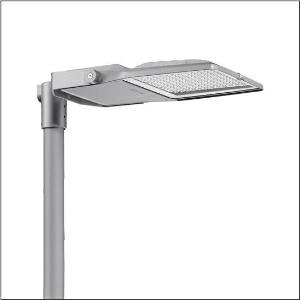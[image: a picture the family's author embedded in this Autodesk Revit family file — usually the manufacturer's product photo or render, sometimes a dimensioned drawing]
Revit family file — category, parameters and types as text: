
# Revit family: floodlight_fl_21_iq_midi___pl64_5xa7782f4e3a_0b41
name_source: partatom
category: Lighting Fixtures
units: mm (PartAtom-declared; Revit-internal decimal feet)

## family parameters
Cut with Voids When Loaded = No
Host = Face
Light Source = No
Part Type = Normal
Room Calculation Point = No
Round Connector Dimension = Use Diameter
Shared = No

## types (1)
- --- (1 x LED, 36050 lm, 270.2 W, 4000K)
    Apparent Load = 270 VA
    CIE Flux Codes = 28 80 98 100 100
    Color Rendering = 70
    Color Temperature = 4000K
    Default Elevation = 1800 mm
    Description = Floodlight FL 21 iQ midi, floodlight, primary light control with lens, of PMMA, primary optical cover: protective disc, of toughened safety glass, transparent, light distribution: PL64, light emission: direct distribution, installation type: surface-mounted, LED, High Power LED, rated luminous flux: 36.050lm, luminous efficacy: 133lm/W, light colour: 740, colour temperature: 4000K, control gear: ECG iQ, control: optimised constant luminous flux control (CLO 2.0), Desk-Remote (wireless, voltage-free reading and setting of iQ features in the workshop via application-optimized NFC function/RFID function), Smart-Wire, Night-Set, Temp-Guard, Auto-Match, Street-Remote, with terminal, 6-pole, mains connection: 220..240V, AC, 50/60Hz, start of lifetime: 270W, end of service life: 287W, reduction: 118W, luminaire housing, of diecast aluminium, powder-coated, Siteco® metallic grey (DB 702S), corrosivity category C5 mid according to DIN EN ISO 12944, sealing non-destructively replaceable, please order mast flange separately, mast bracket, of steel, galvanised, powder-coated, Siteco® metallic grey (DB 702S), protection rating (complete): IP66, insulation class (complete): insulation class II (safety insulation), certification: CE, ENEC, VDE, protection symbol: D, impact resistance: IK08, permissible operating ambient temperature: -40..+40°C, permissible operating ambient temperature for outdoor applications: -40..+50°C, standard: DIN EN 12944, LABS conformity tested according to VDMA 24364:2018-05, packaging unit: 1 piece

Light Distribution: PL64
    Height = 76 mm
    Lamp = 1 x LED
    Lamp Light Flux = 36050 lm
    Lamp Power = 270.2 W
    Lamp count = 1
    Length = 657 mm
    Luminous efficacy = 133 lm/W
    Manufacturer = Siteco
    ModVariant = No
    Model = 5XA7782F4E3A
    Number of Poles = 1
    OnlyDefault = Yes
    Power Factor = 1
    Product Name = Floodlight FL 21 iQ midi | PL64
    Product group = floodlight | pylon annexe
    ProductGroupID = 6200
    Protection Class = Protection class II
    Protection Degree = IP 66
    RLX_Detail_Level = 1
    RLX_Emergency_Light_Flux = 0 lm
    RLX_Emergency_Type = 0
    RLX_Emergency_Type_DB = No
    RlxData = <blob elided: 153925 chars, md5=7fec4c2a>
    Socket = socket
    Standby Power = 0 W
    System Light Flux = 36050 lm
    System Power = 270 W
    Type Comments = factory setting: luminous flux: 100 % | dim-lin: 254 | 620 mA
    Type Image = l_1007123.jpg
    URL = http://relux.com
    VarID = @adj_075411
    Voltage = 0 V
    Weight = 0.00 kg
    Width = 442 mm

## geometry (parser evidence)
native form markers: Blend x4, Sweep x12
no freeform markers — native parametric forms only
